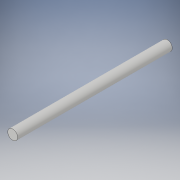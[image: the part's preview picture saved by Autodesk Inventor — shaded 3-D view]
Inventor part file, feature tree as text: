
AUTODESK INVENTOR PART (.ipt)
format: ipt  version: 2018 (Build 220112000, 112)  size: 90,112 bytes
history: native  units: in
note: dims shown in document units (in); Inventor stores cm internally (conversion verified against a paired STEP export)
features: extrude x1, sketch x1
ambient origin geometry x8: Origin, YZ Plane, XZ Plane, XY Plane, X Axis, Y Axis, Z Axis, Center Point
bodies: Solid1 (feature_tree)
feature tree (2):
  extrude  "Extrusion1"  Depth=7.874in TaperAngle=0.0deg
  sketch  "Sketch1"  dims[d0=0.5in d1=7.874in d2=0.0in]
